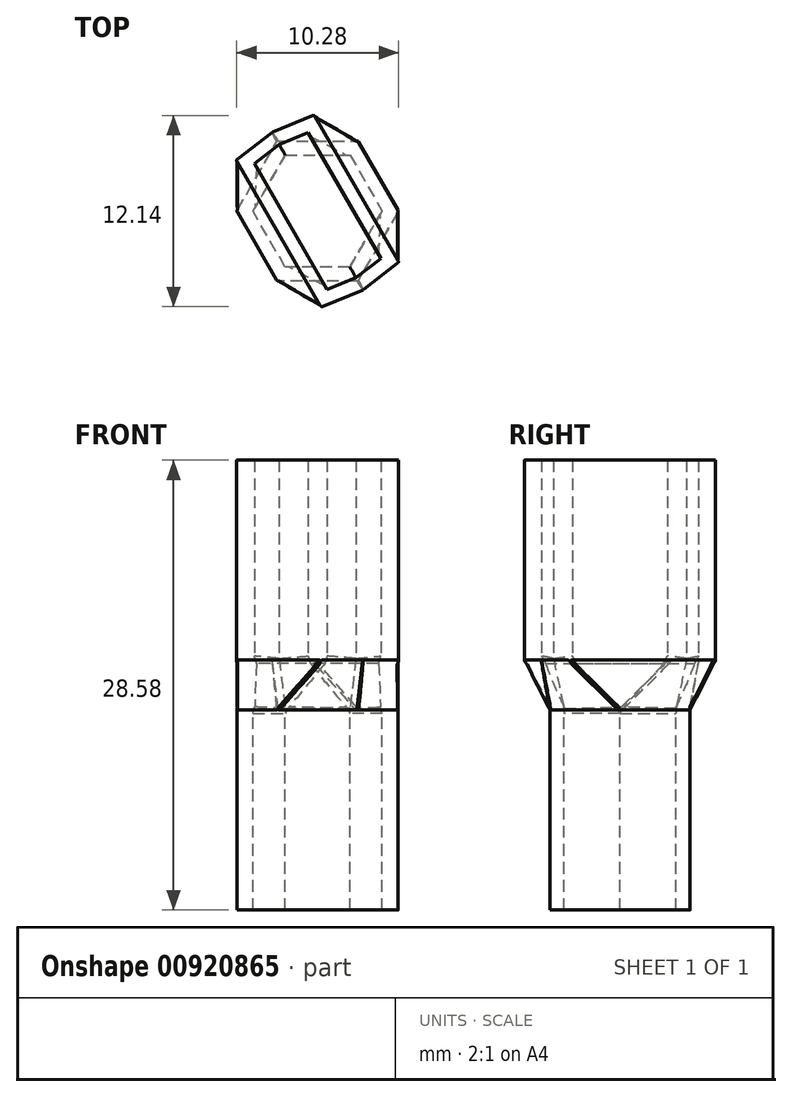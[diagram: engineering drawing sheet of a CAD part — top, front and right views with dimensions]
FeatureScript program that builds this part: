
annotation { "Feature Type Name" : "Feature", "Feature Type Description" : "" }
export const myFeature = defineFeature(function(context is Context, id is Id, definition is map)
    precondition{}
    {
        {
            var Q0;
            Q0=qCreatedBy(makeId("Top.planeOp"),FACE);
            var sketch = newSketch(context, id + "F0", { "sketchPlane" : qUnion([Q0])});
            skCircle(sketch, "E0.cCircle", {"center": v(0, 0) * mm, "radius": 3.56 * mm, "construction": true});
            skLineSegment(sketch, "E0.0", {"start": v(2.05, 3.56) * mm, "end": v(4.1, 0) * mm, "construction": true});
            skLineSegment(sketch, "E0.1", {"start": v(4.1, 0) * mm, "end": v(2.05, -3.56) * mm, "construction": true});
            skLineSegment(sketch, "E0.2", {"start": v(2.05, -3.56) * mm, "end": v(-2.05, -3.56) * mm, "construction": true});
            skLineSegment(sketch, "E0.3", {"start": v(-2.05, -3.56) * mm, "end": v(-4.1, 0) * mm, "construction": true});
            skLineSegment(sketch, "E0.4", {"start": v(-4.1, 0) * mm, "end": v(-2.05, 3.56) * mm, "construction": true});
            skLineSegment(sketch, "E0.5", {"start": v(-2.05, 3.56) * mm, "end": v(2.05, 3.56) * mm, "construction": true});
            skPoint(sketch, "E0.0.midPoint", {"position": v(3.08, 1.78) * mm});
            skLineSegment(sketch, "E1.0", {"start": v(-5.13, 0) * mm, "end": v(-2.57, 4.45) * mm});
            skLineSegment(sketch, "E1.1", {"start": v(2.57, 4.45) * mm, "end": v(5.13, 0) * mm});
            skLineSegment(sketch, "E1.2", {"start": v(5.13, 0) * mm, "end": v(2.57, -4.45) * mm});
            skLineSegment(sketch, "E1.3", {"start": v(-2.57, 4.45) * mm, "end": v(2.57, 4.45) * mm});
            skLineSegment(sketch, "E1.4", {"start": v(2.57, -4.45) * mm, "end": v(-2.57, -4.45) * mm});
            skLineSegment(sketch, "E1.5", {"start": v(-2.57, -4.45) * mm, "end": v(-5.13, 0) * mm});
            skSolve(sketch);
        }
        {
            var Q0;
            Q0 = qSketchRegion(id + "F0", true);
            extrude(context, id + "F1", {"entities" : qUnion([Q0]), "depth" : 12.7 * mm, "offsetDistance" : 25.4 * mm});
        }
        {
            var Q0;
            Q0=makeQuery(id+"F1.opExtrude","CAP_FACE",FACE,{"disambiguationData":[OSD([sQuery(id+"F0.wireOp",EDGE,"E0.0"),sQuery(id+"F0.wireOp",EDGE,"E0.1"),sQuery(id+"F0.wireOp",EDGE,"E0.2"),sQuery(id+"F0.wireOp",EDGE,"E0.3"),sQuery(id+"F0.wireOp",EDGE,"E0.4"),sQuery(id+"F0.wireOp",EDGE,"E0.5"),sQuery(id+"F0.wireOp",EDGE,"E1.0"),sQuery(id+"F0.wireOp",EDGE,"E1.1"),sQuery(id+"F0.wireOp",EDGE,"E1.2"),sQuery(id+"F0.wireOp",EDGE,"E1.3"),sQuery(id+"F0.wireOp",EDGE,"E1.4"),sQuery(id+"F0.wireOp",EDGE,"E1.5")])],"isStart":false});
            cPlane(context, id + "F2", {"entities" : qUnion([Q0]), "cplaneType" : CPlaneType.OFFSET, "offset" : 15.88 * mm, "width" : 152.4 * mm, "height" : 152.4 * mm});
        }
        {
            var Q0;
            Q0=qCreatedBy(id+"F2.planeOp",FACE);
            var sketch = newSketch(context, id + "F3", { "sketchPlane" : qUnion([Q0])});
            skLineSegment(sketch, "E2.bottom", {"start": v(-5.17, 3.25) * mm, "end": v(-0.22, 6.1) * mm});
            skLineSegment(sketch, "E2.top", {"start": v(0.22, -6.1) * mm, "end": v(5.17, -3.25) * mm});
            skLineSegment(sketch, "E2.left", {"start": v(-5.17, 3.25) * mm, "end": v(0.22, -6.1) * mm});
            skLineSegment(sketch, "E2.right", {"start": v(-0.22, 6.1) * mm, "end": v(5.17, -3.25) * mm});
            skPoint(sketch, "E2.middle", {"position": v(0, 0) * mm});
            skSolve(sketch);
        }
        {
            var Q0;
            Q0 = qSketchRegion(id + "F3", true);
            extrude(context, id + "F4", {"entities" : qUnion([Q0]), "oppositeDirection" : true, "depth" : 12.7 * mm, "offsetDistance" : 25.4 * mm});
        }
        {
            var Q0;
            Q0=qCreatedBy(id+"F2.planeOp",FACE);
            var sketch = newSketch(context, id + "F5", { "sketchPlane" : qUnion([Q0])});
            skLineSegment(sketch, "E3", {"start": v(-0.22, 6.1) * mm, "end": v(-2.89, 5) * mm});
            skLineSegment(sketch, "E4", {"start": v(-2.89, 5) * mm, "end": v(-5.17, 3.25) * mm});
            skLineSegment(sketch, "E5", {"start": v(-5.17, 3.25) * mm, "end": v(-0.22, 6.1) * mm});
            skLineSegment(sketch, "E6", {"start": v(5.17, -3.25) * mm, "end": v(0.22, -6.1) * mm});
            skLineSegment(sketch, "E7", {"start": v(0.22, -6.1) * mm, "end": v(2.89, -5) * mm});
            skLineSegment(sketch, "E8", {"start": v(2.89, -5) * mm, "end": v(5.17, -3.25) * mm});
            skSolve(sketch);
        }
        {
            var Q0;
            Q0 = qSketchRegion(id + "F5", true);
            var Q1;
            Q1=makeQuery(id+"F4.opExtrude","CAP_FACE",FACE,{"disambiguationData":[OSD([sQuery(id+"F3.wireOp",EDGE,"E2.bottom"),sQuery(id+"F3.wireOp",EDGE,"E2.top"),sQuery(id+"F3.wireOp",EDGE,"E2.left"),sQuery(id+"F3.wireOp",EDGE,"E2.right")])],"isStart":false});
            extrude(context, id + "F6", {"entities" : qUnion([Q0]), "operationType" : NewBodyOperationType.ADD, "endBound" : BoundingType.UP_TO_SURFACE, "oppositeDirection" : true, "depth" : 25.4 * mm, "endBoundEntityFace" : qUnion([Q1]), "offsetDistance" : 25.4 * mm});
        }
        {
            var Q0;
            Q0=makeQuery(id+"F1.opExtrude","CAP_FACE",FACE,{"disambiguationData":[OSD([sQuery(id+"F0.wireOp",EDGE,"E1.0"),sQuery(id+"F0.wireOp",EDGE,"E1.1"),sQuery(id+"F0.wireOp",EDGE,"E1.2"),sQuery(id+"F0.wireOp",EDGE,"E1.3"),sQuery(id+"F0.wireOp",EDGE,"E1.4"),sQuery(id+"F0.wireOp",EDGE,"E1.5")])],"isStart":false});
            var Q1;
            Q1=makeQuery(id+"F6.boolean.opBoolean","MERGE",FACE,{"derivedFrom":[makeQuery(id+"F4.opExtrude","CAP_FACE",FACE,{"disambiguationData":[OSD([sQuery(id+"F3.wireOp",EDGE,"E2.bottom"),sQuery(id+"F3.wireOp",EDGE,"E2.top"),sQuery(id+"F3.wireOp",EDGE,"E2.left"),sQuery(id+"F3.wireOp",EDGE,"E2.right")])],"isStart":false}),makeQuery(id+"F6.opExtrude","CAP_FACE",FACE,{"disambiguationData":[OSD([sQuery(id+"F5.wireOp",EDGE,"E3"),sQuery(id+"F5.wireOp",EDGE,"E4"),sQuery(id+"F5.wireOp",EDGE,"E5")])],"isStart":false}),makeQuery(id+"F6.opExtrude","CAP_FACE",FACE,{"disambiguationData":[OSD([sQuery(id+"F5.wireOp",EDGE,"E6"),sQuery(id+"F5.wireOp",EDGE,"E7"),sQuery(id+"F5.wireOp",EDGE,"E8")])],"isStart":false})]});
            loft(context, id + "F7", {"operationType" : NewBodyOperationType.ADD, "sheetProfilesArray" : [{ "sheetProfileEntities" : qUnion([Q0]) }, { "sheetProfileEntities" : qUnion([Q1]) }]});
        }
        {
            var Q0;
            Q0=makeQuery(id+"F7.opLoft","SWEPT_EDGE",EDGE,{"disambiguationData":[OSD([sQuery(id+"F0.wireOp",EDGE,"E1.0"),sQuery(id+"F0.wireOp",EDGE,"E1.5"),sQuery(id+"F3.wireOp",EDGE,"E2.bottom"),sQuery(id+"F3.wireOp",EDGE,"E2.left"),sQuery(id+"F5.wireOp",EDGE,"E4"),sQuery(id+"F5.wireOp",EDGE,"E5")])]});
            var Q1;
            Q1=makeQuery(id+"F7.opLoft","SWEPT_EDGE",EDGE,{"disambiguationData":[OSD([sQuery(id+"F0.wireOp",EDGE,"E1.0"),sQuery(id+"F0.wireOp",EDGE,"E1.3"),sQuery(id+"F5.wireOp",EDGE,"E3"),sQuery(id+"F5.wireOp",EDGE,"E4")])]});
            var Q2;
            Q2=makeQuery(id+"F7.opLoft","SWEPT_EDGE",EDGE,{"disambiguationData":[OSD([sQuery(id+"F0.wireOp",EDGE,"E1.1"),sQuery(id+"F0.wireOp",EDGE,"E1.3"),sQuery(id+"F3.wireOp",EDGE,"E2.bottom"),sQuery(id+"F3.wireOp",EDGE,"E2.right"),sQuery(id+"F5.wireOp",EDGE,"E3"),sQuery(id+"F5.wireOp",EDGE,"E5")])]});
            var Q3;
            Q3=makeQuery(id+"F7.opLoft","SWEPT_EDGE",EDGE,{"disambiguationData":[OSD([sQuery(id+"F0.wireOp",EDGE,"E1.1"),sQuery(id+"F0.wireOp",EDGE,"E1.2"),sQuery(id+"F3.wireOp",EDGE,"E2.top"),sQuery(id+"F3.wireOp",EDGE,"E2.right"),sQuery(id+"F5.wireOp",EDGE,"E6"),sQuery(id+"F5.wireOp",EDGE,"E8")])]});
            var Q4;
            Q4=makeQuery(id+"F7.opLoft","SWEPT_EDGE",EDGE,{"disambiguationData":[OSD([sQuery(id+"F0.wireOp",EDGE,"E1.2"),sQuery(id+"F0.wireOp",EDGE,"E1.4"),sQuery(id+"F5.wireOp",EDGE,"E7"),sQuery(id+"F5.wireOp",EDGE,"E8")])]});
            var Q5;
            Q5=makeQuery(id+"F7.opLoft","SWEPT_EDGE",EDGE,{"disambiguationData":[OSD([sQuery(id+"F0.wireOp",EDGE,"E1.4"),sQuery(id+"F0.wireOp",EDGE,"E1.5"),sQuery(id+"F3.wireOp",EDGE,"E2.top"),sQuery(id+"F3.wireOp",EDGE,"E2.left"),sQuery(id+"F5.wireOp",EDGE,"E6"),sQuery(id+"F5.wireOp",EDGE,"E7")])]});
            fillet(context, id + "F8", {"entities" : qUnion([Q0, Q1, Q2, Q3, Q4, Q5]), "radius" : 0.13 * mm, "allowEdgeOverflow" : false});
        }
        {
            var Q0;
            Q0=makeQuery(id+"F1.opExtrude","SWEPT_EDGE",EDGE,{"disambiguationData":[OSD([sQuery(id+"F0.wireOp",EDGE,"E1.4"),sQuery(id+"F0.wireOp",EDGE,"E1.5")])]});
            var Q1;
            Q1=makeQuery(id+"F6.boolean.opBoolean","MERGE",EDGE,{"derivedFrom":[makeQuery(id+"F4.opExtrude","SWEPT_EDGE",EDGE,{"disambiguationData":[OSD([sQuery(id+"F3.wireOp",EDGE,"E2.top"),sQuery(id+"F3.wireOp",EDGE,"E2.left")])]}),makeQuery(id+"F6.opExtrude","SWEPT_EDGE",EDGE,{"disambiguationData":[OSD([sQuery(id+"F5.wireOp",EDGE,"E6"),sQuery(id+"F5.wireOp",EDGE,"E7")])]})]});
            var Q2;
            Q2=makeQuery(id+"F6.opExtrude","SWEPT_EDGE",EDGE,{"disambiguationData":[OSD([sQuery(id+"F5.wireOp",EDGE,"E7"),sQuery(id+"F5.wireOp",EDGE,"E8")])]});
            var Q3;
            Q3=makeQuery(id+"F6.boolean.opBoolean","MERGE",EDGE,{"derivedFrom":[makeQuery(id+"F4.opExtrude","SWEPT_EDGE",EDGE,{"disambiguationData":[OSD([sQuery(id+"F3.wireOp",EDGE,"E2.top"),sQuery(id+"F3.wireOp",EDGE,"E2.right")])]}),makeQuery(id+"F6.opExtrude","SWEPT_EDGE",EDGE,{"disambiguationData":[OSD([sQuery(id+"F5.wireOp",EDGE,"E6"),sQuery(id+"F5.wireOp",EDGE,"E8")])]})]});
            var Q4;
            Q4=makeQuery(id+"F1.opExtrude","SWEPT_EDGE",EDGE,{"disambiguationData":[OSD([sQuery(id+"F0.wireOp",EDGE,"E1.2"),sQuery(id+"F0.wireOp",EDGE,"E1.4")])]});
            var Q5;
            Q5=makeQuery(id+"F1.opExtrude","SWEPT_EDGE",EDGE,{"disambiguationData":[OSD([sQuery(id+"F0.wireOp",EDGE,"E1.1"),sQuery(id+"F0.wireOp",EDGE,"E1.2")])]});
            var Q6;
            Q6=makeQuery(id+"F1.opExtrude","SWEPT_EDGE",EDGE,{"disambiguationData":[OSD([sQuery(id+"F0.wireOp",EDGE,"E1.1"),sQuery(id+"F0.wireOp",EDGE,"E1.3")])]});
            var Q7;
            Q7=makeQuery(id+"F1.opExtrude","SWEPT_EDGE",EDGE,{"disambiguationData":[OSD([sQuery(id+"F0.wireOp",EDGE,"E1.0"),sQuery(id+"F0.wireOp",EDGE,"E1.3")])]});
            var Q8;
            Q8=makeQuery(id+"F1.opExtrude","SWEPT_EDGE",EDGE,{"disambiguationData":[OSD([sQuery(id+"F0.wireOp",EDGE,"E1.0"),sQuery(id+"F0.wireOp",EDGE,"E1.5")])]});
            var Q9;
            Q9=makeQuery(id+"F6.boolean.opBoolean","MERGE",EDGE,{"derivedFrom":[makeQuery(id+"F4.opExtrude","SWEPT_EDGE",EDGE,{"disambiguationData":[OSD([sQuery(id+"F3.wireOp",EDGE,"E2.bottom"),sQuery(id+"F3.wireOp",EDGE,"E2.right")])]}),makeQuery(id+"F6.opExtrude","SWEPT_EDGE",EDGE,{"disambiguationData":[OSD([sQuery(id+"F5.wireOp",EDGE,"E3"),sQuery(id+"F5.wireOp",EDGE,"E5")])]})]});
            var Q10;
            Q10=makeQuery(id+"F6.opExtrude","SWEPT_EDGE",EDGE,{"disambiguationData":[OSD([sQuery(id+"F5.wireOp",EDGE,"E3"),sQuery(id+"F5.wireOp",EDGE,"E4")])]});
            var Q11;
            Q11=makeQuery(id+"F6.boolean.opBoolean","MERGE",EDGE,{"derivedFrom":[makeQuery(id+"F4.opExtrude","SWEPT_EDGE",EDGE,{"disambiguationData":[OSD([sQuery(id+"F3.wireOp",EDGE,"E2.bottom"),sQuery(id+"F3.wireOp",EDGE,"E2.left")])]}),makeQuery(id+"F6.opExtrude","SWEPT_EDGE",EDGE,{"disambiguationData":[OSD([sQuery(id+"F5.wireOp",EDGE,"E4"),sQuery(id+"F5.wireOp",EDGE,"E5")])]})]});
            fillet(context, id + "F9", {"entities" : qUnion([Q0, Q1, Q2, Q3, Q4, Q5, Q6, Q7, Q8, Q9, Q10, Q11]), "radius" : 0.13 * mm, "tangentPropagation" : true, "allowEdgeOverflow" : false});
        }
        {
            var Q0;
            Q0=makeQuery(id+"F6.boolean.opBoolean","MERGE",FACE,{"derivedFrom":[makeQuery(id+"F4.opExtrude","CAP_FACE",FACE,{"disambiguationData":[OSD([sQuery(id+"F3.wireOp",EDGE,"E2.bottom"),sQuery(id+"F3.wireOp",EDGE,"E2.top"),sQuery(id+"F3.wireOp",EDGE,"E2.left"),sQuery(id+"F3.wireOp",EDGE,"E2.right")])],"isStart":true}),makeQuery(id+"F6.opExtrude","CAP_FACE",FACE,{"disambiguationData":[OSD([sQuery(id+"F5.wireOp",EDGE,"E3"),sQuery(id+"F5.wireOp",EDGE,"E4"),sQuery(id+"F5.wireOp",EDGE,"E5")])],"isStart":true}),makeQuery(id+"F6.opExtrude","CAP_FACE",FACE,{"disambiguationData":[OSD([sQuery(id+"F5.wireOp",EDGE,"E6"),sQuery(id+"F5.wireOp",EDGE,"E7"),sQuery(id+"F5.wireOp",EDGE,"E8")])],"isStart":true})]});
            var Q1;
            Q1=makeQuery(id+"F1.opExtrude","CAP_FACE",FACE,{"disambiguationData":[OSD([sQuery(id+"F0.wireOp",EDGE,"E1.0"),sQuery(id+"F0.wireOp",EDGE,"E1.1"),sQuery(id+"F0.wireOp",EDGE,"E1.2"),sQuery(id+"F0.wireOp",EDGE,"E1.3"),sQuery(id+"F0.wireOp",EDGE,"E1.4"),sQuery(id+"F0.wireOp",EDGE,"E1.5")])],"isStart":true});
            shell(context, id + "F10", {"entities" : qUnion([Q0, Q1]), "thickness" : 0.89 * mm});
        }
    });
